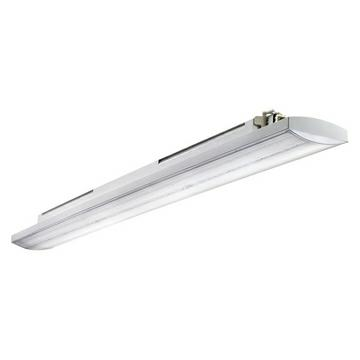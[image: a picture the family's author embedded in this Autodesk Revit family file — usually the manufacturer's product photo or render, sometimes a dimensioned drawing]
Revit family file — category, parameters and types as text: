
# Revit family: Lighting-Industriale-GEWISS-SMART[3]PLUS-PLAFONIERA-LED_TRANSPARENTE_800mm
name_source: partatom
category: Apparecchi per illuminazione
units: mm (PartAtom-declared; Revit-internal decimal feet)

## family parameters
Condiviso = No
Host = Superficie
Punto di calcolo locali = No
Quota connettore circolare = Usa diametro
Sorgente d'illuminazione = Sì
Taglio con vuoti quando caricato = No
Tipo di parte = Normale

## types (1)
- Lighting-Industriale-GEWISS-SMART[3]PLUS-PLAFONIERA-LED_TRANSPARENTE_800mm
    Angolo inclinazione = -90.00°
    Applicazione = Interno
    Carico apparente = 35 VA
    Catalogo = LIGHTING
    Catalogo Serie = SMART[3] PLUS
    Classe di efficienza LED integrati = A ÷ A++
    Classe isolamento = II
    Codice Electrocod = 2434
    Commenti sul wattaggio = 35W
    D_simbolo = 129 mm
    Descrizione = SMART3 PLUS 800 T.W.DALI HE TRASP 9 57
    Emetti da lunghezza linea = 700 mm  [stored 2.29659 ft]
    File diagramma fotometrico = GWS3123AT957.IES
    Filtro dei colori = 16777215
    Ganci = GEWISS  - ALLUMINIO
    Garanzia = 5 anni
    Glow Wire Test = 850°C
    Grado di protezione = IP66/IP69
    IDF = 56b10fca-28fd-4f7f-b1d8-d3c43a13c274
    IDT = a7a40100-d365-495d-870d-5573c78dcb86
    Immagine tipo = GWS3236TC.jpg
    Lampada = LED
    Lampada: = LED
    Lumen output (lm) = 3100
    Lunghezza = 800 mm
    Lunghezza Lampada = 800 mm  [stored 2.62467 ft]
    Modello = GWS3123AT957
    Numero poli = 2
    Potenza di sistema = 26 W
    Produttore = GEWISS S.p.A.
    Prospetto di default = 1219 mm
    Resistenza agli urti = IK08
    SEO = Plafoniera
    Scheda Tecnica = https://www.gewiss.com
    Schermo = Trasparente
    Schermo. = Gewiss - Led Acceso
    Stampa 1_100 = Sì
    Stampa 1_200 = No
    Struttura = GEWISS - SMART 3 - GRIGIO
    Temperatura di colore = 5700 K (CRI > 90)
    Temperatura di colore: = 5700 K (CRI > 90)
    Temperatura di funzionamento = -25 +50 °C
    Temperatura di utilizzo = -25 +50 °C
    Tensione = 220-240 V
    Tipologia = DALI
    Tipologia sorgente luminosa = LED - Non sostituibile
    URL = https://www.gewiss.com
    Variazione temperatura colore lampada con luminosità attenuata = <Nessuno>
    Versione file RFA = 20.0

note: [stored X ft] marks values corroborated as IEEE doubles in the binary element streams (Revit-internal decimal feet)
